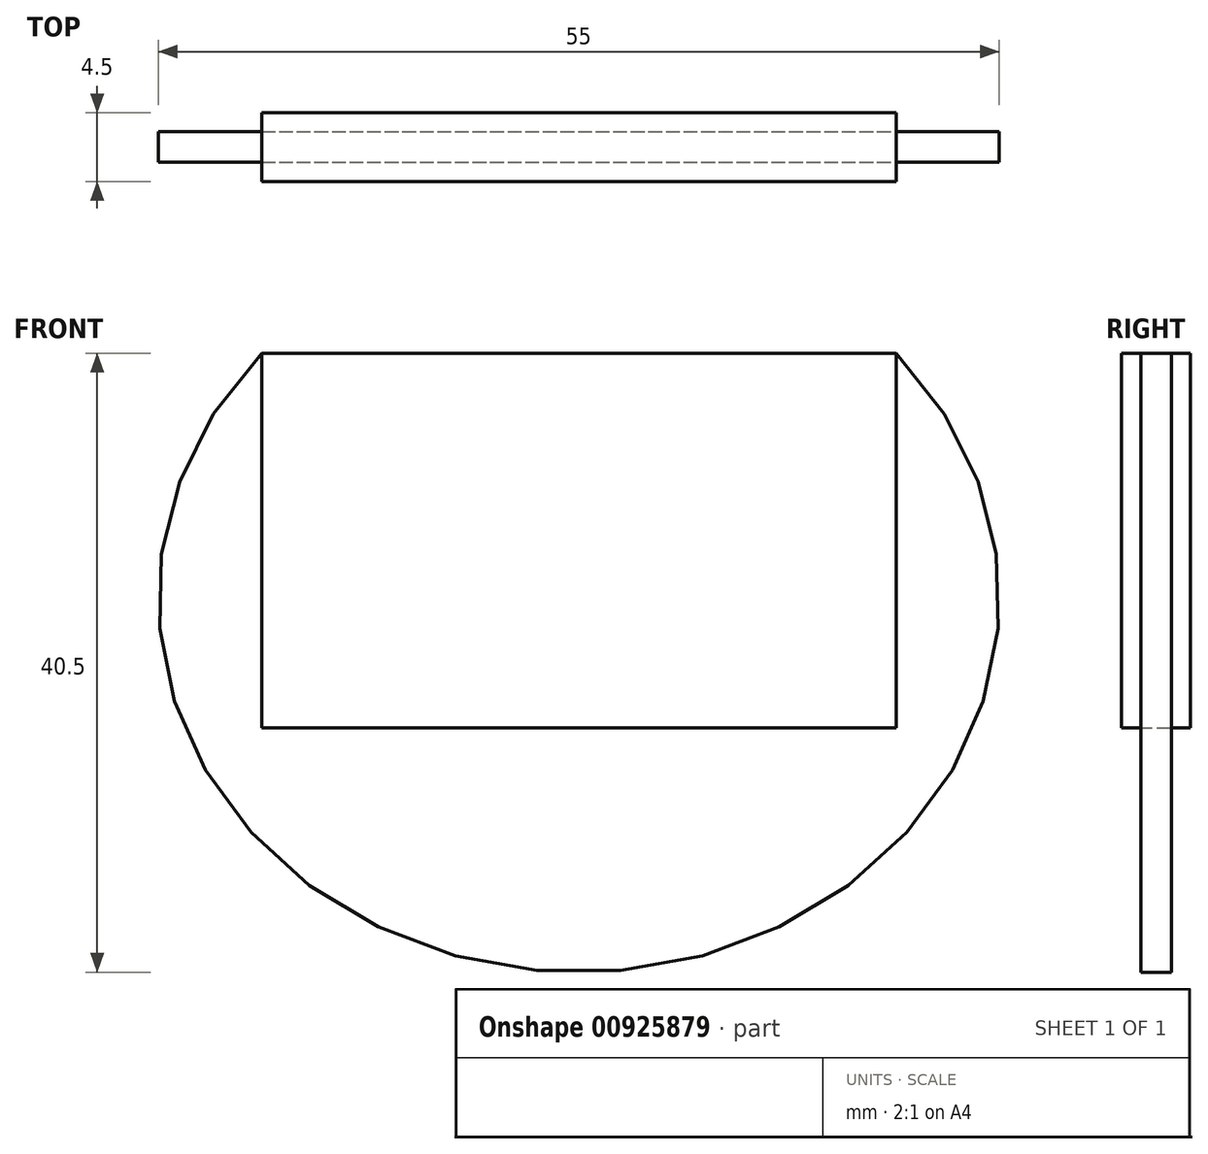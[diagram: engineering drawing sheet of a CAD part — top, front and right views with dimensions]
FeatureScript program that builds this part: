
annotation { "Feature Type Name" : "Feature", "Feature Type Description" : "" }
export const myFeature = defineFeature(function(context is Context, id is Id, definition is map)
    precondition{}
    {
        {
            var Q0;
            Q0=qCreatedBy(makeId("Front.planeOp"),FACE);
            var sketch = newSketch(context, id + "F0", { "sketchPlane" : qUnion([Q0])});
            skLineSegment(sketch, "E0.bottom", {"start": v(-17.36, 17.99) * mm, "end": v(24.14, 17.99) * mm});
            skLineSegment(sketch, "E0.top", {"start": v(-17.36, -6.51) * mm, "end": v(24.14, -6.51) * mm});
            skLineSegment(sketch, "E0.left", {"start": v(-17.36, 17.99) * mm, "end": v(-17.36, -6.51) * mm});
            skLineSegment(sketch, "E0.right", {"start": v(24.14, 17.99) * mm, "end": v(24.14, -6.51) * mm});
            skArc(sketch, "E1", {"start": v(-17.36, 17.99) * mm, "mid": v(-12.7, -21.53) * mm, "end": v(24.14, -6.51) * mm});
            skLineSegment(sketch, "E2", {"start": v(0, 0) * mm, "end": v(-17.36, 17.99) * mm, "construction": true});
            skLineSegment(sketch, "E3", {"start": v(0, 0) * mm, "end": v(24.14, -6.51) * mm, "construction": true});
            skSolve(sketch);
        }
        {
            var Q0;
            Q0=qCreatedBy(makeId("Front.planeOp"),FACE);
            var sketch = newSketch(context, id + "F1", { "sketchPlane" : qUnion([Q0])});
            skEllipticalArc(sketch, "E4", {});
            skLineSegment(sketch, "E5.bottom", {"start": v(-20.75, 12.25) * mm, "end": v(20.75, 12.25) * mm});
            skLineSegment(sketch, "E5.top", {"start": v(-20.75, -12.25) * mm, "end": v(20.75, -12.25) * mm});
            skLineSegment(sketch, "E5.left", {"start": v(-20.75, 12.25) * mm, "end": v(-20.75, -12.25) * mm});
            skLineSegment(sketch, "E5.right", {"start": v(20.75, 12.25) * mm, "end": v(20.75, -12.25) * mm});
            skPoint(sketch, "E6", {"position": v(0, 12.25) * mm});
            skPoint(sketch, "E7", {"position": v(20.75, 0) * mm});
            skPoint(sketch, "E8", {"position": v(-27.17, 0) * mm});
            skPoint(sketch, "E9", {"position": v(0, -28.25) * mm});
            const initialGuessF1  = {"E4": [0, -0.0037971371282830213, 1, 0, 0.0275, 0.02445286287171698, 2.4257575271865486, 0.7158351264032461]};
            skSetInitialGuess(sketch, initialGuessF1);
            skSolve(sketch);
        }
        {
            var Q0;
            Q0=makeQuery(id+"F1.imprint","IMPRINT",FACE,{"disambiguationData":[TD([[makeQuery(id+"F1.imprint","IMPRINT",EDGE,{"derivedFrom":sQuery(id+"F1.wireOp",EDGE,"E5.bottom")}),-1.0]])]});
            extrude(context, id + "F2", {"entities" : qUnion([Q0]), "endBound" : BoundingType.SYMMETRIC, "depth" : 4.5 * mm, "offsetDistance" : 25 * mm});
        }
        {
            var Q0;
            Q0=makeQuery(id+"F1.imprint","IMPRINT",FACE,{"disambiguationData":[TD([[makeQuery(id+"F1.imprint","IMPRINT",EDGE,{"derivedFrom":sQuery(id+"F1.wireOp",EDGE,"E4")}),1.0]])]});
            extrude(context, id + "F3", {"entities" : qUnion([Q0]), "endBound" : BoundingType.SYMMETRIC, "depth" : 2 * mm, "offsetDistance" : 25 * mm});
        }
    });
